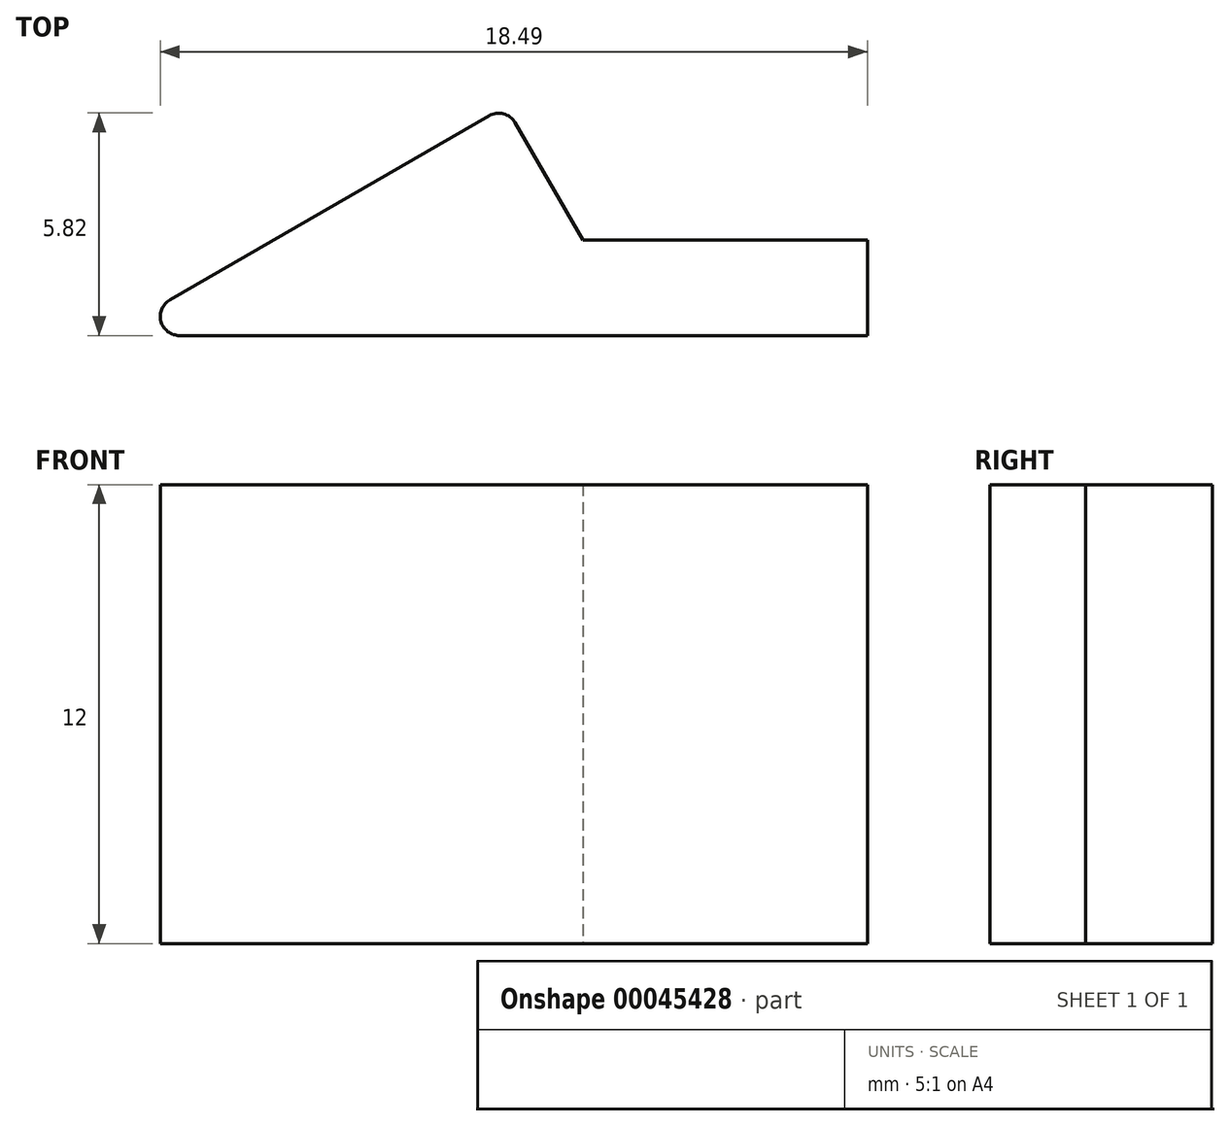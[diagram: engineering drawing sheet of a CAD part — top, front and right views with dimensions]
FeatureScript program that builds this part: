
annotation { "Feature Type Name" : "Feature", "Feature Type Description" : "" }
export const myFeature = defineFeature(function(context is Context, id is Id, definition is map)
    precondition{}
    {
        {
            var Q0;
            Q0=qCreatedBy(makeId("Top.planeOp"),FACE);
            var sketch = newSketch(context, id + "F0", { "sketchPlane" : qUnion([Q0])});
            skLineSegment(sketch, "E0", {"start": v(0, 0) * mm, "end": v(-13.86, 0) * mm});
            skLineSegment(sketch, "E1", {"start": v(-13.86, 0) * mm, "end": v(-3.46, 6) * mm});
            skLineSegment(sketch, "E2", {"start": v(-3.46, 6) * mm, "end": v(0, 0) * mm});
            skLineSegment(sketch, "E3", {"start": v(-3.46, 6) * mm, "end": v(-3.46, 0) * mm, "construction": true});
            skSolve(sketch);
        }
        {
            var Q0;
            Q0=qSketchRegion(id+"F0",true);
            extrude(context, id + "F1", {"entities" : qUnion([Q0]), "depth" : 12 * mm});
        }
        {
            var Q0;
            Q0=qCreatedBy(makeId("Right.planeOp"),FACE);
            cPlane(context, id + "F2", {"entities" : qUnion([Q0]), "cplaneType" : CPlaneType.OFFSET, "offset" : 3.46 * mm, "oppositeDirection" : true, "width" : 150 * mm, "height" : 150 * mm});
        }
        {
            var Q0;
            Q0=qCreatedBy(id+"F2.planeOp",FACE);
            var sketch = newSketch(context, id + "F3", { "sketchPlane" : qUnion([Q0])});
            skLineSegment(sketch, "E4.bottom", {"start": v(0, 0) * mm, "end": v(2.5, 0) * mm});
            skLineSegment(sketch, "E4.top", {"start": v(0, 12) * mm, "end": v(2.5, 12) * mm});
            skLineSegment(sketch, "E4.left", {"start": v(0, 0) * mm, "end": v(0, 12) * mm});
            skLineSegment(sketch, "E4.right", {"start": v(2.5, 0) * mm, "end": v(2.5, 12) * mm});
            skSolve(sketch);
        }
        {
            var Q0;
            Q0=qSketchRegion(id+"F3",true);
            extrude(context, id + "F4", {"entities" : qUnion([Q0]), "operationType" : NewBodyOperationType.ADD, "depth" : 9.46 * mm});
        }
        {
            var Q0;
            Q0=makeQuery(id+"F1.opExtrude","SWEPT_EDGE",EDGE,{"disambiguationData":[OSD([sQuery(id+"F0.wireOp",EDGE,"E1"),sQuery(id+"F0.wireOp",EDGE,"E2")])]});
            var Q1;
            Q1=makeQuery(id+"F1.opExtrude","SWEPT_EDGE",EDGE,{"disambiguationData":[OSD([sQuery(id+"F0.wireOp",EDGE,"E0"),sQuery(id+"F0.wireOp",EDGE,"E1")])]});
            fillet(context, id + "F5", {"entities" : qUnion([Q0, Q1]), "radius" : .5 * mm, "tangentPropagation" : true, "allowEdgeOverflow" : false});
        }
    });
